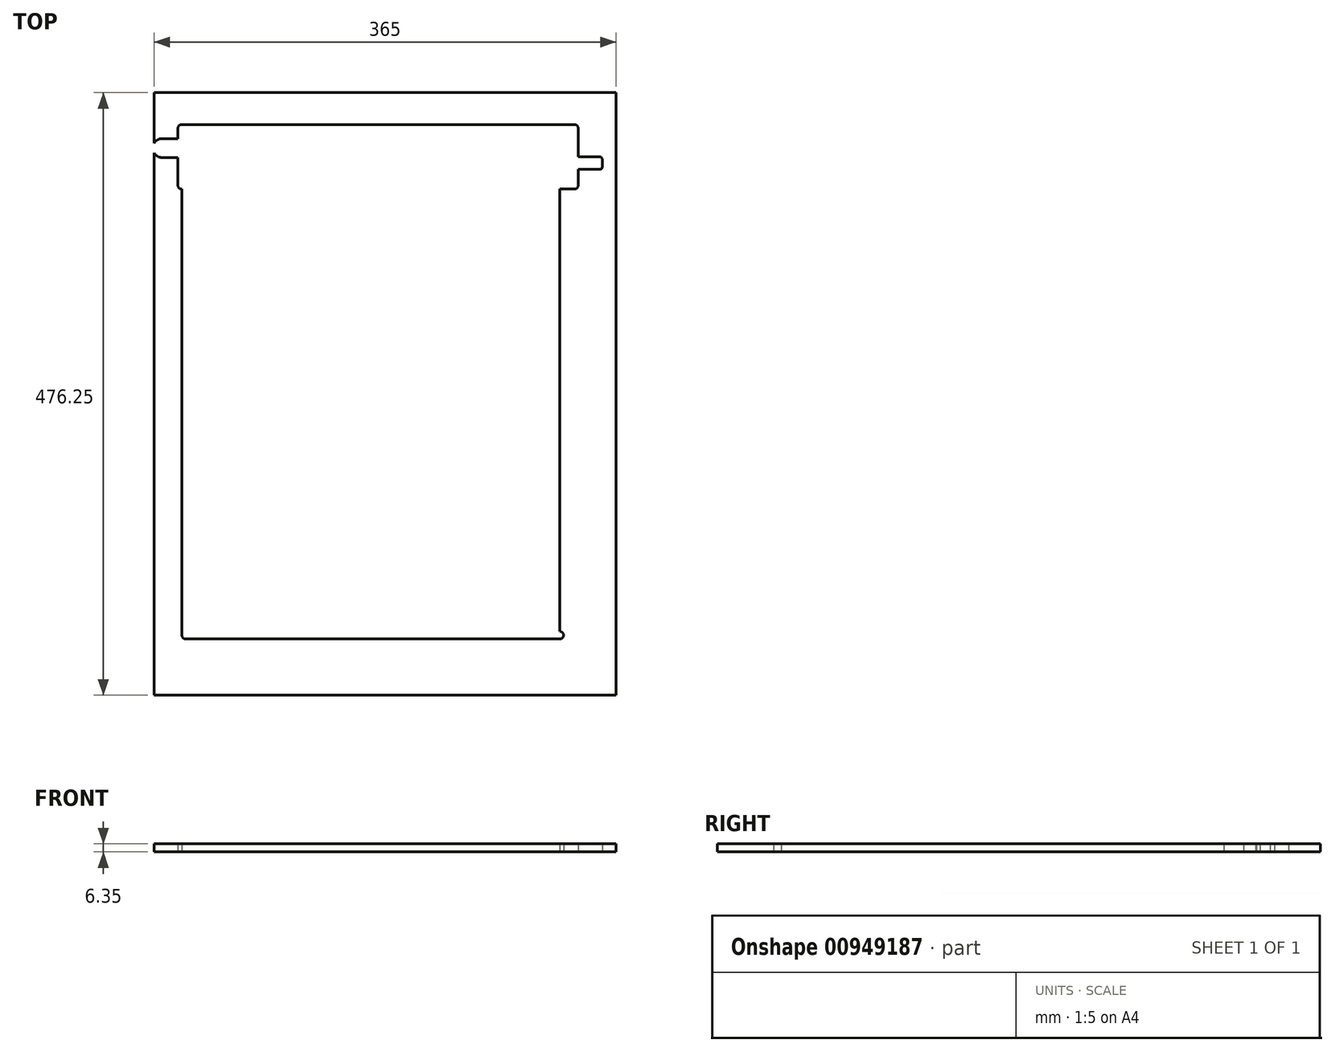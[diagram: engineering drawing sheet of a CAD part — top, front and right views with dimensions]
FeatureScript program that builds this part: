
annotation { "Feature Type Name" : "Feature", "Feature Type Description" : "" }
export const myFeature = defineFeature(function(context is Context, id is Id, definition is map)
    precondition{}
    {
        {
            var Q0;
            Q0=qCreatedBy(makeId("Top.planeOp"),FACE);
            var sketch = newSketch(context, id + "F0", { "sketchPlane" : qUnion([Q0])});
            skLineSegment(sketch, "E0.bottom", {"start": v(0, 0) * mm, "end": v(-365, 0) * mm});
            skLineSegment(sketch, "E0.left", {"start": v(0, 0) * mm, "end": v(0, -107.95) * mm});
            skLineSegment(sketch, "E0.right", {"start": v(-365, 0) * mm, "end": v(-365, -107.95) * mm});
            skLineSegment(sketch, "E1.bottom", {"start": v(-343.07, -25.2) * mm, "end": v(-33, -25.2) * mm});
            skPoint(sketch, "E2.visualSharp", {"position": v(-346.07, -25.2) * mm});
            skArc(sketch, "E2.filletArc", {"start": v(-343.07, -25.2) * mm, "mid": v(-345.2, -26.08) * mm, "end": v(-346.07, -28.2) * mm});
            skPoint(sketch, "E3.visualSharp", {"position": v(-41.27, -25.2) * mm});
            skArc(sketch, "E3.filletArc", {"start": v(-30, -28.2) * mm, "mid": v(-30.88, -26.08) * mm, "end": v(-33, -25.2) * mm});
            skPoint(sketch, "E4.visualSharp", {"position": v(-41.27, -76.2) * mm});
            skArc(sketch, "E4.filletArc", {"start": v(-33, -76.2) * mm, "mid": v(-30.88, -75.32) * mm, "end": v(-30, -73.2) * mm});
            skPoint(sketch, "E5.visualSharp", {"position": v(-346.07, -76.2) * mm});
            skArc(sketch, "E5.filletArc", {"start": v(-346.07, -73.2) * mm, "mid": v(-345.2, -75.32) * mm, "end": v(-343.07, -76.2) * mm});
            skLineSegment(sketch, "E6", {"start": v(-342.9, -107.95) * mm, "end": v(-342.9, -76.2) * mm});
            skLineSegment(sketch, "E7", {"start": v(-342.9, -76.2) * mm, "end": v(-343.07, -76.2) * mm});
            skLineSegment(sketch, "E8", {"start": v(-44.45, -76.2) * mm, "end": v(-33, -76.2) * mm});
            skLineSegment(sketch, "E9", {"start": v(-346.07, -36.28) * mm, "end": v(-358.57, -36.28) * mm});
            skLineSegment(sketch, "E10", {"start": v(-346.07, -51.28) * mm, "end": v(-358.57, -51.28) * mm});
            skArc(sketch, "E11", {"start": v(-358.57, -36.28) * mm, "mid": v(-366.07, -43.78) * mm, "end": v(-358.57, -51.28) * mm});
            skLineSegment(sketch, "E12", {"start": v(-30, -50.7) * mm, "end": v(-13, -50.7) * mm});
            skLineSegment(sketch, "E13", {"start": v(-30, -60.7) * mm, "end": v(-13, -60.7) * mm});
            skLineSegment(sketch, "E14", {"start": v(-346.07, -28.2) * mm, "end": v(-346.07, -36.28) * mm});
            skLineSegment(sketch, "E15", {"start": v(-346.07, -51.28) * mm, "end": v(-346.07, -73.2) * mm});
            skLineSegment(sketch, "E16", {"start": v(-30, -28.2) * mm, "end": v(-30, -50.7) * mm});
            skLineSegment(sketch, "E17", {"start": v(-30, -60.7) * mm, "end": v(-30, -73.2) * mm});
            skLineSegment(sketch, "E18", {"start": v(-365, -107.95) * mm, "end": v(-365, -476.25) * mm});
            skLineSegment(sketch, "E19", {"start": v(-365, -476.25) * mm, "end": v(0, -476.25) * mm});
            skLineSegment(sketch, "E20", {"start": v(0, -476.25) * mm, "end": v(0, -107.95) * mm});
            skLineSegment(sketch, "E21", {"start": v(-342.9, -107.95) * mm, "end": v(-342.9, -428.8) * mm});
            skLineSegment(sketch, "E22", {"start": v(-339.9, -431.8) * mm, "end": v(-44.5, -431.8) * mm});
            skLineSegment(sketch, "E23", {"start": v(-11, -52.7) * mm, "end": v(-11, -58.7) * mm});
            skPoint(sketch, "E24.visualSharp", {"position": v(-11, -50.7) * mm});
            skArc(sketch, "E24.filletArc", {"start": v(-11, -52.7) * mm, "mid": v(-11.59, -51.29) * mm, "end": v(-13, -50.7) * mm});
            skPoint(sketch, "E25.visualSharp", {"position": v(-11, -60.7) * mm});
            skArc(sketch, "E25.filletArc", {"start": v(-13, -60.7) * mm, "mid": v(-11.59, -60.11) * mm, "end": v(-11, -58.7) * mm});
            skPoint(sketch, "E26.visualSharp", {"position": v(-44.45, -431.8) * mm});
            skArc(sketch, "E26.filletArc", {"start": v(-44.5, -431.8) * mm, "mid": v(-41.5, -428.83) * mm, "end": v(-44.45, -425.8) * mm});
            skPoint(sketch, "E27.visualSharp", {"position": v(-342.9, -431.8) * mm});
            skArc(sketch, "E27.filletArc", {"start": v(-342.9, -428.8) * mm, "mid": v(-342.02, -430.92) * mm, "end": v(-339.9, -431.8) * mm});
            skLineSegment(sketch, "E28", {"start": v(-44.45, -76.2) * mm, "end": v(-44.45, -425.8) * mm});
            skSolve(sketch);
        }
        {
            var Q0;
            Q0=makeQuery(id+"F0.imprint","IMPRINT",FACE,{"disambiguationData":[TD([[makeQuery(id+"F0.imprint","IMPRINT",EDGE,{"derivedFrom":sQuery(id+"F0.wireOp",EDGE,"E0.bottom")}),1.0]])]});
            extrude(context, id + "F1", {"entities" : qUnion([Q0]), "depth" : 6.35 * mm, "offsetDistance" : 25 * mm});
        }
    });
